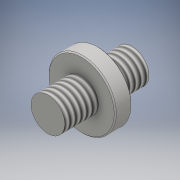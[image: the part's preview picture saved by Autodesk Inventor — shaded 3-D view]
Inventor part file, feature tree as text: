
AUTODESK INVENTOR PART (.ipt)
format: ipt  version: 2016 (Build 200138000, 138)  size: 139,264 bytes
history: native  units: mm
features: extrude x3, sketch x3, thread x2, chamfer x2, projected_geometry x1
ambient origin geometry x8: Origin, YZ Plane, XZ Plane, XY Plane, X Axis, Y Axis, Z Axis, Center Point
bodies: Solid1 (feature_tree)
feature tree (11):
  extrude  "Extrusion1"  Depth=1.5mm TaperAngle=0.0deg
  extrude  "Extrusion2"  Depth=3.0mm TaperAngle=0.0deg
  extrude  "Extrusion3"  Depth=3.0mm TaperAngle=0.0deg
  thread  "Thread1"  [1 undecoded]
  thread  "Thread2"  [1 undecoded]
  chamfer  "Chamfer1"  Distance=0.1mm Angle=45.0deg
  chamfer  "Chamfer2"  Distance=0.1mm Angle=45.0deg
  sketch  "Sketch1"  dims[d0=6.0mm d1=1.5mm d2=0.0mm]
  sketch  "Sketch2"  dims[d3=3.0mm d4=3.0mm d5=0.0mm]
  projected_geometry  "Projected Loop1"
  sketch  "Sketch3"  dims[d6=3.0mm d7=3.0mm d8=0.0mm d9=10.0mm d10=0.0mm d11=10.0mm d12=0.0mm d13=0.1mm d14=2.0mm d15=45.0deg d16=0.1mm d17=2.0mm d18=45.0deg]
note: 2 required parameter values undecoded (feature->parameter linkage not recoverable at this tier; creation-order binding heuristic only, values carry confidence <= 0.55)
